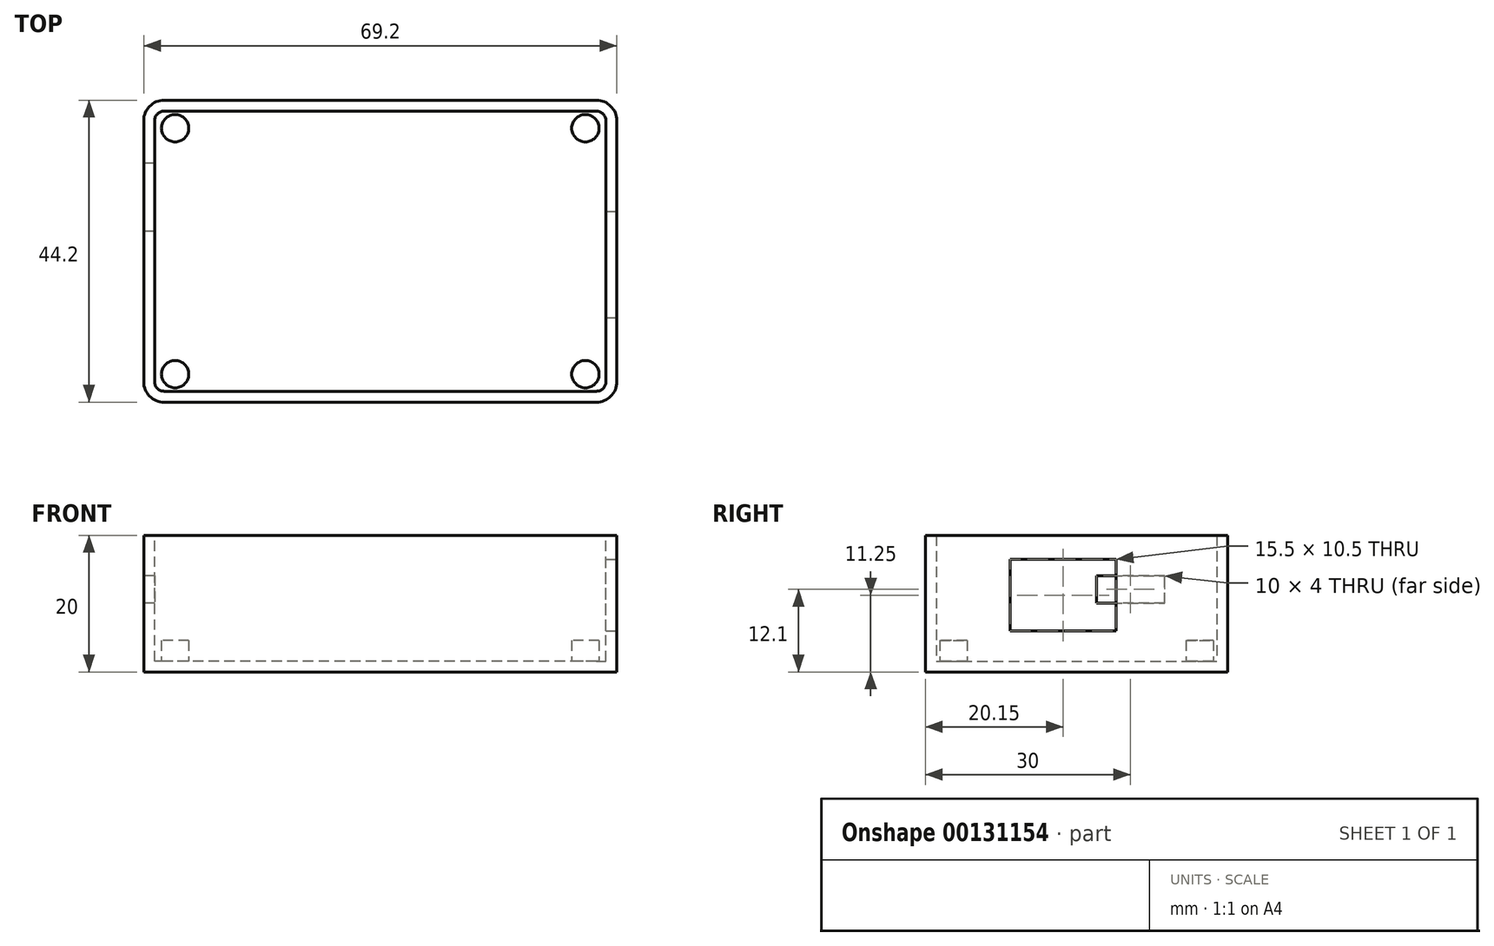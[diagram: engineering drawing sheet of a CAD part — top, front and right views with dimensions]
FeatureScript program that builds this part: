
annotation { "Feature Type Name" : "Feature", "Feature Type Description" : "" }
export const myFeature = defineFeature(function(context is Context, id is Id, definition is map)
    precondition{}
    {
        {
            var Q0;
            Q0=qCreatedBy(makeId("Top.planeOp"),FACE);
            var sketch = newSketch(context, id + "F0", { "sketchPlane" : qUnion([Q0])});
            skLineSegment(sketch, "E0.bottom", {"start": v(34.6, -22.1) * mm, "end": v(-34.6, -22.1) * mm});
            skLineSegment(sketch, "E0.top", {"start": v(34.6, 22.1) * mm, "end": v(-34.6, 22.1) * mm});
            skLineSegment(sketch, "E0.left", {"start": v(34.6, -22.1) * mm, "end": v(34.6, 22.1) * mm});
            skLineSegment(sketch, "E0.right", {"start": v(-34.6, -22.1) * mm, "end": v(-34.6, 22.1) * mm});
            skPoint(sketch, "E0.middle", {"position": v(0, 0) * mm});
            skSolve(sketch);
        }
        {
            var Q0;
            Q0=makeQuery(id+"F0.imprint","IMPRINT",FACE,{"disambiguationData":[TD([[makeQuery(id+"F0.imprint","IMPRINT",EDGE,{"derivedFrom":sQuery(id+"F0.wireOp",EDGE,"E0.bottom")}),-1.0]])]});
            extrude(context, id + "F1", {"entities" : qUnion([Q0]), "depth" : 20 * mm});
        }
        {
            var Q0;
            Q0=makeQuery(id+"F1.opExtrude","SWEPT_EDGE",EDGE,{"disambiguationData":[OSD([sQuery(id+"F0.wireOp",EDGE,"E0.bottom"),sQuery(id+"F0.wireOp",EDGE,"E0.left")])]});
            var Q1;
            Q1=makeQuery(id+"F1.opExtrude","SWEPT_EDGE",EDGE,{"disambiguationData":[OSD([sQuery(id+"F0.wireOp",EDGE,"E0.top"),sQuery(id+"F0.wireOp",EDGE,"E0.left")])]});
            var Q2;
            Q2=makeQuery(id+"F1.opExtrude","SWEPT_EDGE",EDGE,{"disambiguationData":[OSD([sQuery(id+"F0.wireOp",EDGE,"E0.top"),sQuery(id+"F0.wireOp",EDGE,"E0.right")])]});
            var Q3;
            Q3=makeQuery(id+"F1.opExtrude","SWEPT_EDGE",EDGE,{"disambiguationData":[OSD([sQuery(id+"F0.wireOp",EDGE,"E0.bottom"),sQuery(id+"F0.wireOp",EDGE,"E0.right")])]});
            fillet(context, id + "F2", {"entities" : qUnion([Q0, Q1, Q2, Q3]), "radius" : 3 * mm, "tangentPropagation" : true, "allowEdgeOverflow" : false});
        }
        {
            var Q0;
            Q0=makeQuery(id+"F1.opExtrude","CAP_FACE",FACE,{"disambiguationData":[OSD([sQuery(id+"F0.wireOp",EDGE,"E0.bottom"),sQuery(id+"F0.wireOp",EDGE,"E0.top"),sQuery(id+"F0.wireOp",EDGE,"E0.left"),sQuery(id+"F0.wireOp",EDGE,"E0.right")])],"isStart":false});
            shell(context, id + "F3", {"entities" : qUnion([Q0]), "thickness" : 1.6 * mm});
        }
        {
            var Q0;
            Q0=makeQuery(id+"F3.opShell","OFFSET_FACE",FACE,{"disambiguationData":[OSD([sQuery(id+"F0.wireOp",EDGE,"E0.bottom"),sQuery(id+"F0.wireOp",EDGE,"E0.top"),sQuery(id+"F0.wireOp",EDGE,"E0.left"),sQuery(id+"F0.wireOp",EDGE,"E0.right")])]});
            var sketch = newSketch(context, id + "F4", { "sketchPlane" : qUnion([Q0])});
            skLineSegment(sketch, "E1.bottom", {"start": v(30, -18) * mm, "end": v(-30, -18) * mm, "construction": true});
            skLineSegment(sketch, "E1.top", {"start": v(30, 18) * mm, "end": v(-30, 18) * mm, "construction": true});
            skLineSegment(sketch, "E1.left", {"start": v(30, -18) * mm, "end": v(30, 18) * mm, "construction": true});
            skLineSegment(sketch, "E1.right", {"start": v(-30, -18) * mm, "end": v(-30, 18) * mm, "construction": true});
            skPoint(sketch, "E1.middle", {"position": v(0, 0) * mm});
            skCircle(sketch, "E2", {"center": v(-30, 18) * mm, "radius": 2 * mm});
            skCircle(sketch, "E3", {"center": v(-30, -18) * mm, "radius": 2 * mm});
            skCircle(sketch, "E4", {"center": v(30, 18) * mm, "radius": 2 * mm});
            skCircle(sketch, "E5", {"center": v(30, -18) * mm, "radius": 2 * mm});
            skSolve(sketch);
        }
        {
            var Q0;
            Q0=makeQuery(id+"F4.imprint","IMPRINT",FACE,{"disambiguationData":[TD([[makeQuery(id+"F4.imprint","IMPRINT",EDGE,{"derivedFrom":sQuery(id+"F4.wireOp",EDGE,"E2")}),1.0]])]});
            var Q1;
            Q1=makeQuery(id+"F4.imprint","IMPRINT",FACE,{"disambiguationData":[TD([[makeQuery(id+"F4.imprint","IMPRINT",EDGE,{"derivedFrom":sQuery(id+"F4.wireOp",EDGE,"E4")}),1.0]])]});
            var Q2;
            Q2=makeQuery(id+"F4.imprint","IMPRINT",FACE,{"disambiguationData":[TD([[makeQuery(id+"F4.imprint","IMPRINT",EDGE,{"derivedFrom":sQuery(id+"F4.wireOp",EDGE,"E5")}),1.0]])]});
            var Q3;
            Q3=makeQuery(id+"F4.imprint","IMPRINT",FACE,{"disambiguationData":[TD([[makeQuery(id+"F4.imprint","IMPRINT",EDGE,{"derivedFrom":sQuery(id+"F4.wireOp",EDGE,"E3")}),1.0]])]});
            var Q4;
            Q4=sQuery(id+"F4.wireOp",EDGE,"E4");
            var Q5;
            Q5=sQuery(id+"F4.wireOp",EDGE,"E2");
            var Q6;
            Q6=sQuery(id+"F4.wireOp",EDGE,"E3");
            var Q7;
            Q7=sQuery(id+"F4.wireOp",EDGE,"E5");
            extrude(context, id + "F5", {"entities" : qUnion([Q0, Q1, Q2, Q3]), "operationType" : NewBodyOperationType.ADD, "surfaceEntities" : qUnion([Q4, Q5, Q6, Q7]), "depth" : 3 * mm});
        }
        {
            var Q0;
            Q0=makeQuery(id+"F1.opExtrude","SWEPT_FACE",FACE,{"disambiguationData":[OSD([sQuery(id+"F0.wireOp",EDGE,"E0.left")])]});
            var sketch = newSketch(context, id + "F6", { "sketchPlane" : qUnion([Q0])});
            skLineSegment(sketch, "E6.bottom", {"start": v(5.8, 6) * mm, "end": v(-9.7, 6) * mm});
            skLineSegment(sketch, "E6.top", {"start": v(5.8, 16.5) * mm, "end": v(-9.7, 16.5) * mm});
            skLineSegment(sketch, "E6.left", {"start": v(5.8, 6) * mm, "end": v(5.8, 16.5) * mm});
            skLineSegment(sketch, "E6.right", {"start": v(-9.7, 6) * mm, "end": v(-9.7, 16.5) * mm});
            skPoint(sketch, "E6.middle", {"position": v(-1.95, 11.25) * mm});
            skSolve(sketch);
        }
        {
            var Q0;
            Q0=makeQuery(id+"F6.imprint","IMPRINT",FACE,{"disambiguationData":[TD([[makeQuery(id+"F6.imprint","IMPRINT",EDGE,{"derivedFrom":sQuery(id+"F6.wireOp",EDGE,"E6.bottom")}),-1.0]])]});
            extrude(context, id + "F7", {"entities" : qUnion([Q0]), "operationType" : NewBodyOperationType.REMOVE, "endBound" : BoundingType.UP_TO_NEXT, "oppositeDirection" : true, "depth" : 25 * mm});
        }
        {
            var Q0;
            Q0=makeQuery(id+"F1.opExtrude","SWEPT_FACE",FACE,{"disambiguationData":[OSD([sQuery(id+"F0.wireOp",EDGE,"E0.right")])]});
            var sketch = newSketch(context, id + "F8", { "sketchPlane" : qUnion([Q0])});
            skLineSegment(sketch, "E7.bottom", {"start": v(-2.9, 10.1) * mm, "end": v(-12.9, 10.1) * mm});
            skLineSegment(sketch, "E7.top", {"start": v(-2.9, 14.1) * mm, "end": v(-12.9, 14.1) * mm});
            skLineSegment(sketch, "E7.left", {"start": v(-2.9, 10.1) * mm, "end": v(-2.9, 14.1) * mm});
            skLineSegment(sketch, "E7.right", {"start": v(-12.9, 10.1) * mm, "end": v(-12.9, 14.1) * mm});
            skPoint(sketch, "E7.middle", {"position": v(-7.9, 12.1) * mm});
            skSolve(sketch);
        }
        {
            var Q0;
            Q0=makeQuery(id+"F8.imprint","IMPRINT",FACE,{"disambiguationData":[TD([[makeQuery(id+"F8.imprint","IMPRINT",EDGE,{"derivedFrom":sQuery(id+"F8.wireOp",EDGE,"E7.bottom")}),-1.0]])]});
            extrude(context, id + "F9", {"entities" : qUnion([Q0]), "operationType" : NewBodyOperationType.REMOVE, "endBound" : BoundingType.UP_TO_NEXT, "oppositeDirection" : true, "depth" : 25 * mm});
        }
    });
